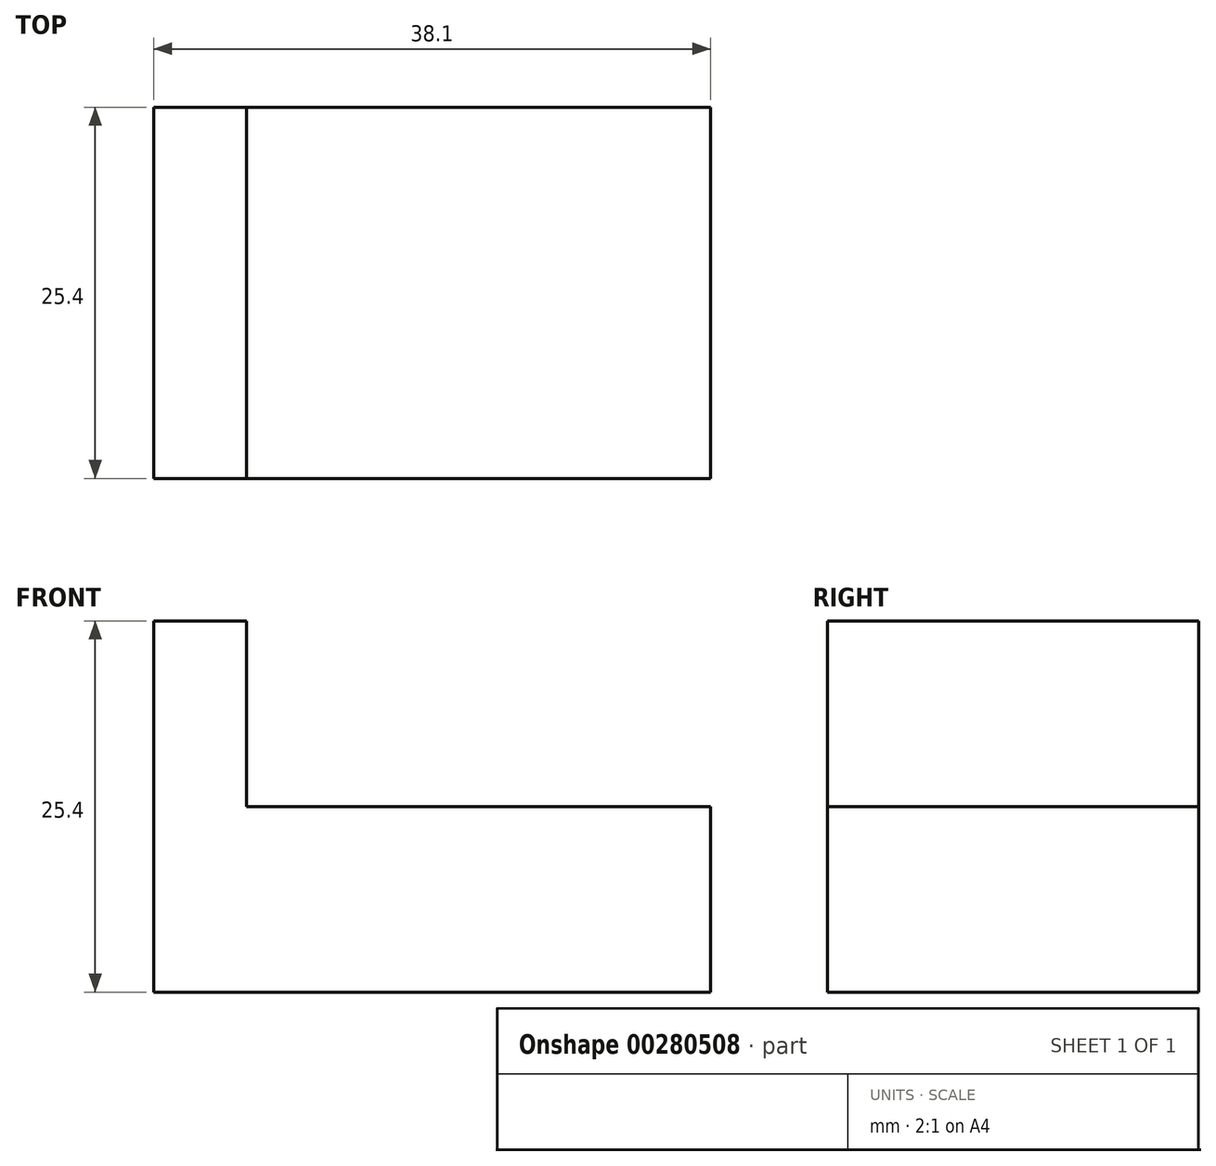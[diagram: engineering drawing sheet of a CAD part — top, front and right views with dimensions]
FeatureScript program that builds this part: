
annotation { "Feature Type Name" : "Feature", "Feature Type Description" : "" }
export const myFeature = defineFeature(function(context is Context, id is Id, definition is map)
    precondition{}
    {
        {
            var Q0;
            Q0=qCreatedBy(makeId("Front.planeOp"),FACE);
            var sketch = newSketch(context, id + "F0", { "sketchPlane" : qUnion([Q0])});
            skLineSegment(sketch, "E0", {"start": v(0, 0) * mm, "end": v(0, 25.4) * mm});
            skLineSegment(sketch, "E1", {"start": v(0, 25.4) * mm, "end": v(6.35, 25.4) * mm});
            skLineSegment(sketch, "E2", {"start": v(6.35, 25.4) * mm, "end": v(6.35, 12.7) * mm});
            skLineSegment(sketch, "E3", {"start": v(38.1, 12.7) * mm, "end": v(6.35, 12.7) * mm});
            skLineSegment(sketch, "E4", {"start": v(38.1, 12.7) * mm, "end": v(38.1, 0) * mm});
            skLineSegment(sketch, "E5", {"start": v(38.1, 0) * mm, "end": v(0, 0) * mm});
            skSolve(sketch);
        }
        {
            var Q0;
            Q0=makeQuery(id+"F0.imprint","IMPRINT",FACE,{"disambiguationData":[TD([[makeQuery(id+"F0.imprint","IMPRINT",EDGE,{"derivedFrom":sQuery(id+"F0.wireOp",EDGE,"E0")}),-1.0]])]});
            extrude(context, id + "F1", {"entities" : qUnion([Q0]), "depth" : 25.4 * mm});
        }
    });
